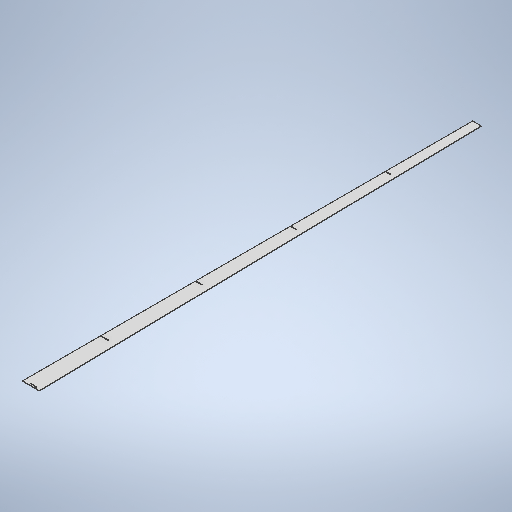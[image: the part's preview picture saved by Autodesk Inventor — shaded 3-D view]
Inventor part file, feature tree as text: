
AUTODESK INVENTOR PART (.ipt)
format: ipt  version: 2025 (Build 290162010, 162A)  size: 768,512 bytes
history: native  units: mm
features: other x3, sketch x3, projected_geometry x2, sheet_metal_op x1, extrude x1
ambient origin geometry x8: Origin, YZ Plane, XZ Plane, XY Plane, X Axis, Y Axis, Z Axis, Center Point
bodies: Solid1 (feature_tree)
feature tree (10):
  sheet_metal_op  "Face1"
  extrude  "Extrusion1"  Depth=200.0mm
  other  "Mark1"
  sketch  "Sketch1"  dims[d2=3.0mm]
  other  "Plate1"
  sketch  "Sketch2"  dims[d3=2400.0mm d4=2950.0mm d5=50.0mm d6=100.0mm d7=50.0mm d9=135.0deg d10=950.0mm d11=1150.0mm d12=23.743743mm d13=50.0mm d14=100.0mm d15=212.132034mm d17=55.0mm d18=200.0mm d19=200.0mm d20=200.0mm]
  projected_geometry  "Projected Loop1"
  sketch  "Sketch3"  dims[d26=3.0mm d29=0.0mm d30=0.0mm d34=46.326363mm d36=41.228805mm d39=36.144545mm d42=31.053636mm d43=560.0mm d44=3.2mm d45=560.0mm d46=3.2mm d47=560.0mm d48=3.2mm d49=3.2mm d50=2705.0mm d52=460.0mm d53=50.0mm]
  projected_geometry  "Projected Loop2"
  other  "Definition1"
